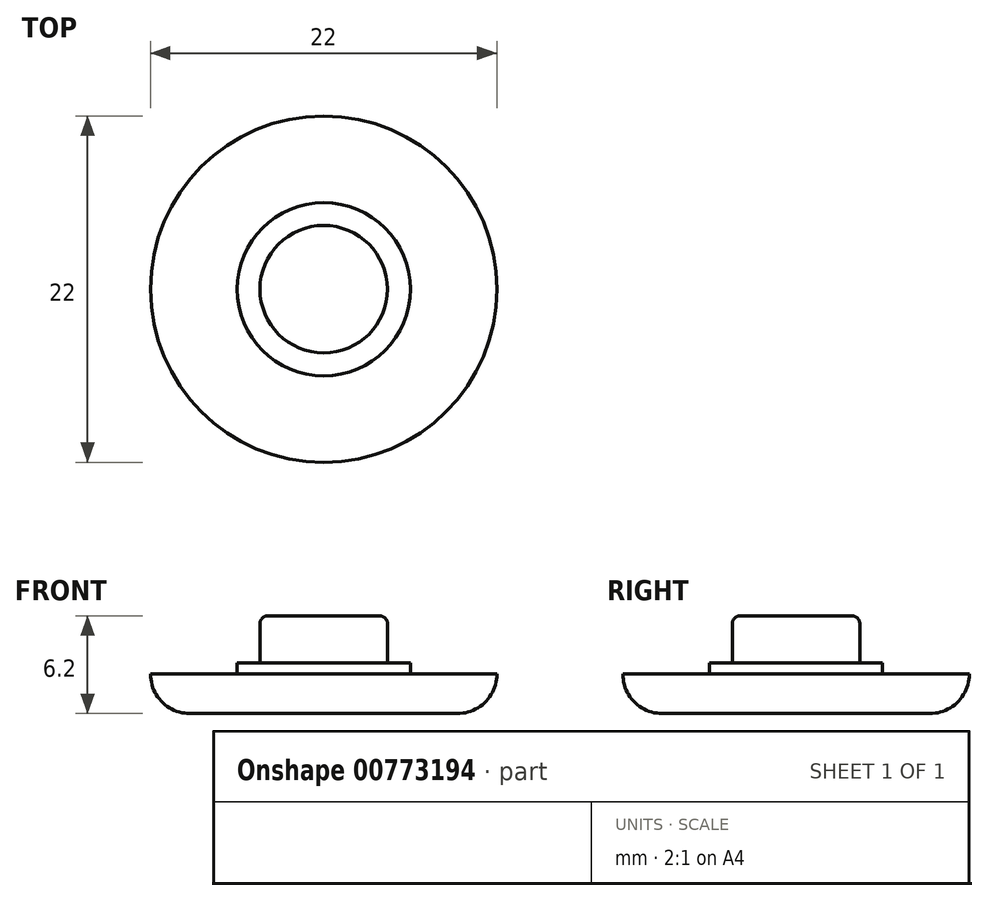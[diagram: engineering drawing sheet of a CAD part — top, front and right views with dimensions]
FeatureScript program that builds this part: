
annotation { "Feature Type Name" : "Feature", "Feature Type Description" : "" }
export const myFeature = defineFeature(function(context is Context, id is Id, definition is map)
    precondition{}
    {
        {
            var Q0;
            Q0=qCreatedBy(makeId("Top.planeOp"),FACE);
            var sketch = newSketch(context, id + "F0", { "sketchPlane" : qUnion([Q0])});
            skCircle(sketch, "E0", {"center": v(0, 0) * mm, "radius": 11 * mm});
            skCircle(sketch, "E1", {"center": v(0, 0) * mm, "radius": 5.5 * mm});
            skCircle(sketch, "E2", {"center": v(0, 0) * mm, "radius": 4.05 * mm});
            skSolve(sketch);
        }
        {
            var Q0;
            Q0=makeQuery(id+"F0.imprint","IMPRINT",FACE,{"disambiguationData":[TD([[makeQuery(id+"F0.imprint","IMPRINT",EDGE,{"derivedFrom":sQuery(id+"F0.wireOp",EDGE,"E0")}),1.0]])]});
            extrude(context, id + "F1", {"entities" : qUnion([Q0]), "depth" : 2.5 * mm, "offsetDistance" : 25 * mm});
        }
        {
            var Q0;
            Q0=makeQuery(id+"F0.imprint","IMPRINT",FACE,{"disambiguationData":[TD([[makeQuery(id+"F0.imprint","IMPRINT",EDGE,{"derivedFrom":sQuery(id+"F0.wireOp",EDGE,"E1")}),1.0]])]});
            extrude(context, id + "F2", {"entities" : qUnion([Q0]), "operationType" : NewBodyOperationType.ADD, "depth" : 3.2 * mm, "offsetDistance" : 25 * mm});
        }
        {
            var Q0;
            Q0=makeQuery(id+"F0.imprint","IMPRINT",FACE,{"disambiguationData":[TD([[makeQuery(id+"F0.imprint","IMPRINT",EDGE,{"derivedFrom":sQuery(id+"F0.wireOp",EDGE,"E2")}),1.0]])]});
            extrude(context, id + "F3", {"entities" : qUnion([Q0]), "operationType" : NewBodyOperationType.ADD, "depth" : 6.2 * mm, "offsetDistance" : 25 * mm});
        }
        {
            var Q0;
            Q0=makeQuery(id+"F1.opExtrude","CAP_EDGE",EDGE,{"disambiguationData":[OSD([sQuery(id+"F0.wireOp",EDGE,"E0")])],"isStart":true});
            fillet(context, id + "F4", {"entities" : qUnion([Q0]), "radius" : 2.5 * mm, "tangentPropagation" : true, "allowEdgeOverflow" : false});
        }
        {
            var Q0;
            Q0=makeQuery(id+"F3.opExtrude","CAP_EDGE",EDGE,{"disambiguationData":[OSD([sQuery(id+"F0.wireOp",EDGE,"E2")])],"isStart":false});
            fillet(context, id + "F5", {"entities" : qUnion([Q0]), "radius" : (0.5) * mm, "tangentPropagation" : true, "allowEdgeOverflow" : false});
        }
    });
